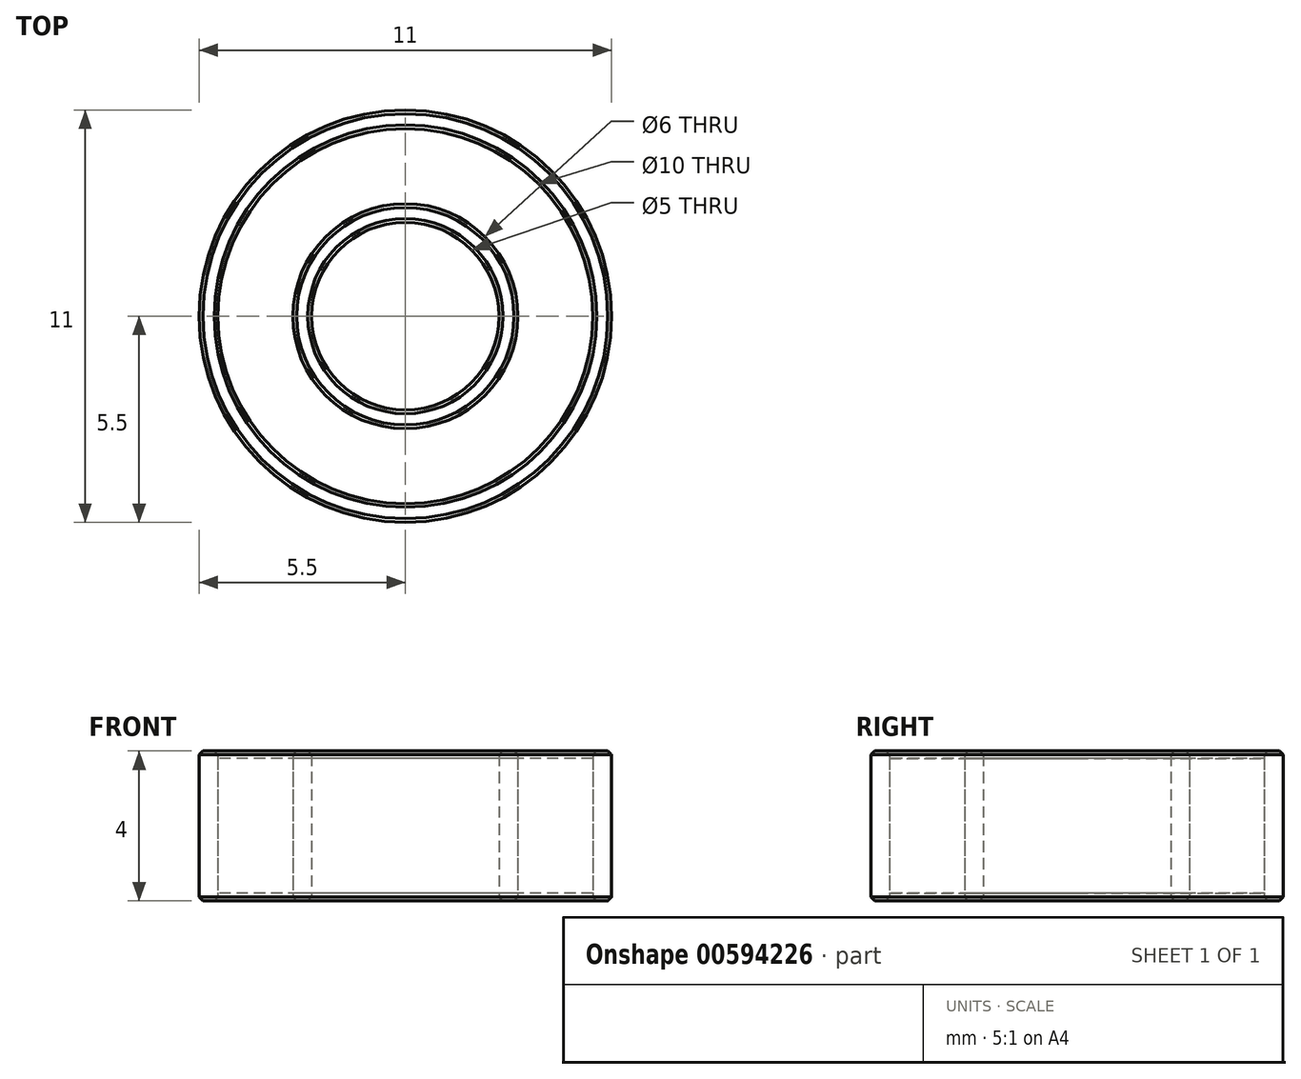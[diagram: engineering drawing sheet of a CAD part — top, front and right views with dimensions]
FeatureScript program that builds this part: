
annotation { "Feature Type Name" : "Feature", "Feature Type Description" : "" }
export const myFeature = defineFeature(function(context is Context, id is Id, definition is map)
    precondition{}
    {
        {
            var Q0;
            Q0=qCreatedBy(makeId("Top.planeOp"),FACE);
            var sketch = newSketch(context, id + "F0", { "sketchPlane" : qUnion([Q0])});
            skCircle(sketch, "E0", {"center": v(0, 0) * mm, "radius": 5.5 * mm});
            skCircle(sketch, "E1", {"center": v(0, 0) * mm, "radius": 2.5 * mm});
            skCircle(sketch, "E2.0", {"center": v(0, 0) * mm, "radius": 5 * mm});
            skCircle(sketch, "E3.0", {"center": v(0, 0) * mm, "radius": 3 * mm});
            skSolve(sketch);
        }
        {
            var Q0;
            Q0=makeQuery(id+"F0.imprint","IMPRINT",FACE,{"disambiguationData":[TD([[makeQuery(id+"F0.imprint","IMPRINT",EDGE,{"derivedFrom":sQuery(id+"F0.wireOp",EDGE,"E1")}),-1.0]])]});
            var Q1;
            Q1=makeQuery(id+"F0.imprint","IMPRINT",FACE,{"disambiguationData":[TD([[makeQuery(id+"F0.imprint","IMPRINT",EDGE,{"derivedFrom":sQuery(id+"F0.wireOp",EDGE,"E0")}),1.0]])]});
            extrude(context, id + "F1", {"entities" : qUnion([Q0, Q1]), "depth" : 4 * mm, "offsetDistance" : 25 * mm});
        }
        {
            var Q0;
            Q0=makeQuery(id+"F0.imprint","IMPRINT",FACE,{"disambiguationData":[TD([[makeQuery(id+"F0.imprint","IMPRINT",EDGE,{"derivedFrom":sQuery(id+"F0.wireOp",EDGE,"E2.0")}),1.0]])]});
            extrude(context, id + "F2", {"entities" : qUnion([Q0]), "depth" : 3.8 * mm, "hasSecondDirection" : true, "secondDirectionOppositeDirection" : false, "secondDirectionDepth" : 0.2 * mm, "offsetDistance" : 25 * mm});
        }
        {
            var Q0;
            {var subQ0=sQuery(id+"F0.wireOp",EDGE,"E0");Q0=makeQuery(id+"F0BHlAFDJWVW7Y7_1.boolean.opBoolean","MERGE",FACE,{"derivedFrom":[makeQuery(id+"F1.opExtrude","CAP_FACE",FACE,{"disambiguationData":[OSD([subQ0,sQuery(id+"F0.wireOp",EDGE,"E2.0")])],"isStart":true}),makeQuery(id+"F0BHlAFDJWVW7Y7_1.opExtrude","CAP_FACE",FACE,{"disambiguationData":[OSD([sQuery(id+"F0.wireOp",EDGE,"MePryiGi-OmUY-C7yO-MmJH-qqiRuWpCLKw8"),subQ0])],"isStart":true})]});}
            var Q1;
            Q1=makeQuery(id+"F1.opExtrude","CAP_FACE",FACE,{"disambiguationData":[OSD([sQuery(id+"F0.wireOp",EDGE,"E1"),sQuery(id+"F0.wireOp",EDGE,"E3.0")])],"isStart":true});
            var Q2;
            Q2=makeQuery(id+"F1.opExtrude","CAP_FACE",FACE,{"disambiguationData":[OSD([sQuery(id+"F0.wireOp",EDGE,"E0"),sQuery(id+"F0.wireOp",EDGE,"E2.0")])],"isStart":false});
            var Q3;
            Q3=makeQuery(id+"F1.opExtrude","CAP_FACE",FACE,{"disambiguationData":[OSD([sQuery(id+"F0.wireOp",EDGE,"E1"),sQuery(id+"F0.wireOp",EDGE,"E3.0")])],"isStart":false});
            var Q4;
            Q4=makeQuery(id+"F0BHlAFDJWVW7Y7_1.opExtrude","CAP_EDGE",EDGE,{"disambiguationData":[OSD([sQuery(id+"F0.wireOp",EDGE,"MePryiGi-OmUY-C7yO-MmJH-qqiRuWpCLKw8")])],"isStart":false});
            chamfer(context, id + "F3", {"entities" : qUnion([Q0, Q1, Q2, Q3, Q4]), "width" : 0.1 * mm, "tangentPropagation" : true});
        }
    });
